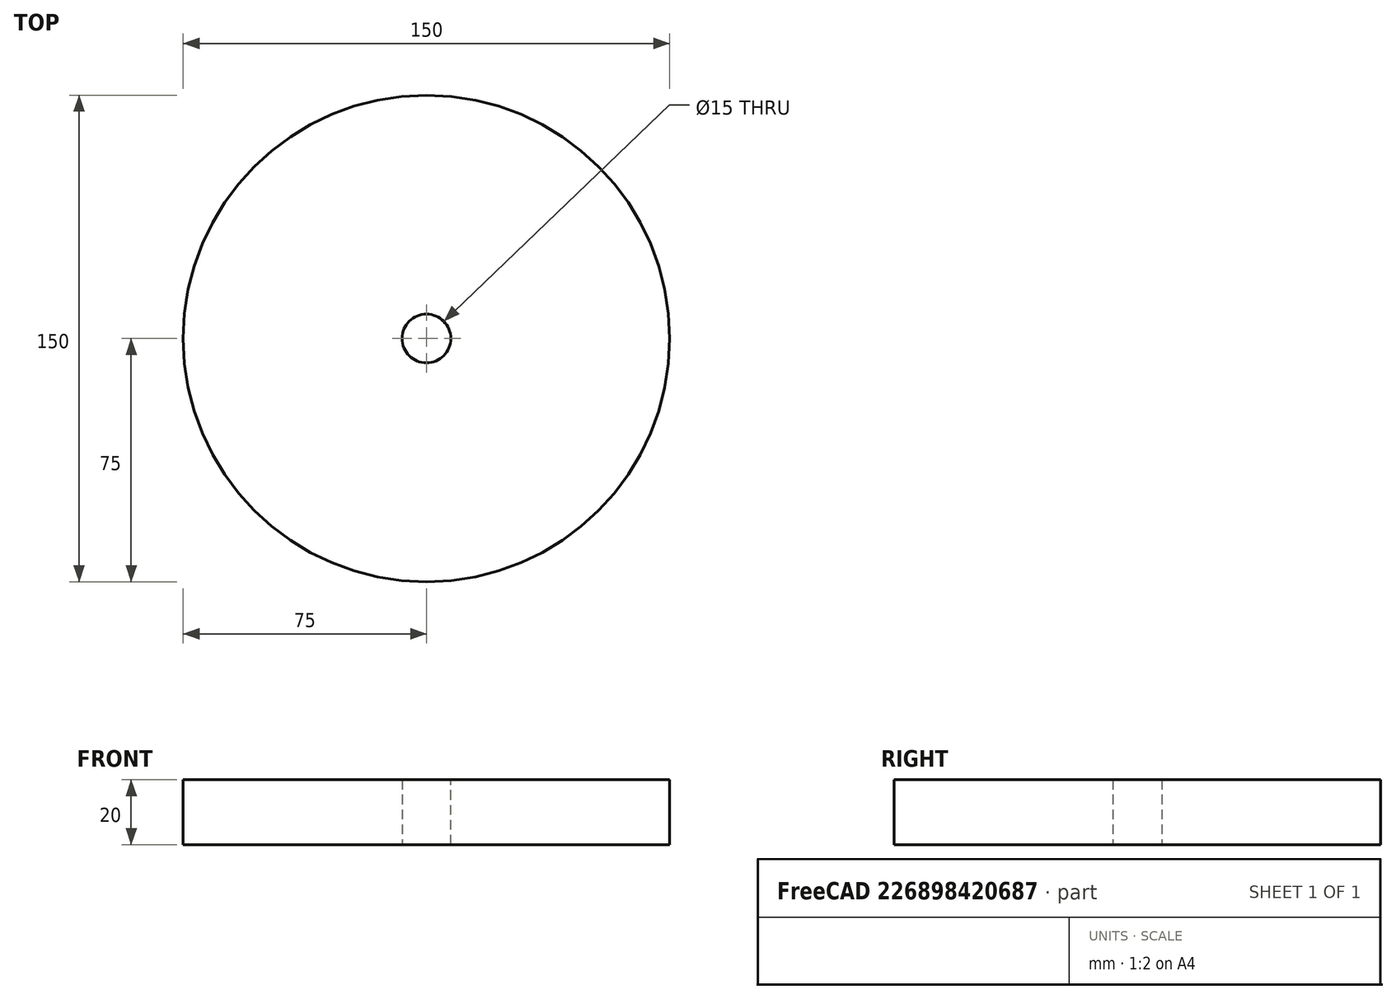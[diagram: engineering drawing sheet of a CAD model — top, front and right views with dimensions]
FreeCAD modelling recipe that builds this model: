
FCSTD DOCUMENT  (FreeCAD 0.18R4 (GitTag))
Label: Base
License: All rights reserved
LicenseURL: http://en.wikipedia.org/wiki/All_rights_reserved
objects: Drawing::FeatureViewPart×3, App::Part×1, Sketcher::SketchObject×1, PartDesign::Pad×1, PartDesign::Body×1, Drawing::FeaturePage×1, Part::Feature×1
note: 5 computed .brp shape members not serialized (recipe doc carries the construction recipe); baked Part::Feature solids carry a one-line shape summary decoded from their .brp

FEATURE [App::Part] Part  label="Base"
  Origin = -> Origin
FEATURE [Sketcher::SketchObject] Sketch
  MapMode = 5
  Support = -> [XY_Plane001]
  sketch-geometry (2):
    g0: Circle CenterX=0 CenterY=0 CenterZ=0 NormalX=0 NormalY=0 NormalZ=1 AngleXU=0 Radius=75
    g1: Circle CenterX=0 CenterY=0 CenterZ=0 NormalX=0 NormalY=0 NormalZ=1 AngleXU=0 Radius=7.5
  constraints (4):
    c: Coincident(g0,g-1)
    c: Coincident(g1,g0)
    c: Diameter(g1) = 15
    c: Diameter(g0) = 150
FEATURE [PartDesign::Pad] Pad
  Length = 20
  Length2 = 100
  Profile = -> Sketch
  Type = 0
FEATURE [PartDesign::Body] Body
  Group = -> [Sketch,Pad]
  Origin = -> Origin001
  Tip = -> Pad
FEATURE [Drawing::FeatureViewPart] Ortho  label="Ortho_0_0"
  Direction = (1,0,0)
  HiddenWidth = 0.15
  LineWidth = 0.35
  Rotation = -90
  ShowHiddenLines = true
  ShowSmoothLines = false
  Source = -> Body
  Tolerance = 0.05
  ViewResult = <blob: 3359 chars omitted>
  Visible = false
  X = 118.36
  Y = 211.298
FEATURE [Drawing::FeatureViewPart] Ortho001  label="Ortho_0_1"
  Direction = (0,0,1)
  HiddenWidth = 0.15
  LineWidth = 0.35
  Rotation = 90
  ShowHiddenLines = true
  ShowSmoothLines = false
  Source = -> Body
  Tolerance = 0.05
  ViewResult = <g id="Ortho_0_1"\n   transform="rotate(90,118.36,100.596) translate(118.36,100.596) scale(1,1)"\n  >\n<g   fill="none"\n   stroke="rgb(0, 0, 0)"\n   stroke-dasharray="0.2,0.1)"\n   stroke-linecap="butt"\n   stroke-linejoin="miter"\n   stroke-width="0.150000"\n   transform="scale(1,-1)"\n  >\n<circle cx ="0" cy ="0" r ="75" /><circle cx ="0" cy ="0" r ="7.5" /></g>\n<g   fill="none"\n   stroke="rgb(0, 0, 0)"\n   stroke-linecap="butt"\n   stroke-linejoin="miter"\n   stroke-width="0.350000"\n   transform="scale(1,-1)"\n  >\n<circle cx ="0" cy ="0" r ="75" /><circle cx ="0" cy ="0" r ="7.5" /></g>\n</g>
  Visible = false
  X = 118.36
  Y = 100.596
FEATURE [Drawing::FeatureViewPart] Ortho002  label="Ortho_1_1"
  Direction = (0.57735,0.57735,0.57735)
  HiddenWidth = 0.15
  LineWidth = 0.35
  Rotation = 120
  ShowHiddenLines = true
  ShowSmoothLines = false
  Source = -> Body
  Tolerance = 0.05
  ViewResult = <g id="Ortho_1_1"\n   transform="rotate(120,301.704,108.792) translate(301.704,108.792) scale(1,1)"\n  >\n<g   fill="none"\n   stroke="rgb(0, 0, 0)"\n   stroke-dasharray="0.2,0.1)"\n   stroke-linecap="butt"\n   stroke-linejoin="miter"\n   stroke-width="0.150000"\n   transform="scale(1,-1)"\n  >\n<path d="M-37.5 64.9519 A75 43.3013 120 0 1 37.5 -64.9519" />\n<path d="M5.3033 -3.06186 A7.5 4.33013 120 0 1 -3.75 6.49519" />\n<path d="M-3.75 6.49519 A7.5 4.33013 120 0 1 3.75 -6.49519" />\n<path d="M3.75 -6.49519 A7.5 4.33013 120 0 1 5.3033 -3.06186" />\n</g>\n<g   fill="none"\n   stroke="rgb(0, 0, 0)"\n   stroke-dasharray="0.02,0.1)"\n   stroke-linecap="butt"\n   stroke-linejoin="miter"\n   stroke-width="0.150000"\n   transform="scale(1,-1)"\n  >\n<path id= "1" d=" M -10.3921 -14.6602 L 3.75 -6.49519 " />\n<path id= "2" d=" M -17.8921 -1.66978 L -3.75 6.49519 " />\n</g>\n<g   fill="none"\n   stroke="rgb(0, 0, 0)"\n   stroke-linecap="butt"\n   stroke-linejoin="miter"\n   stroke-width="0.350000"\n   transform="scale(1,-1)"\n  >\n<path id= "1" d=" M 23.3579 -73.1169 L 37.5 -64.9519 " />\n<path id= "2" d=" M -51.6421 56.7869 L -37.5 64.9519 " />\n</g>\n<g   fill="none"\n   stroke="rgb(0, 0, 0)"\n   stroke-linecap="butt"\n   stroke-linejoin="miter"\n   stroke-width="0.350000"\n   transform="scale(1,-1)"\n  >\n<path d="M53.033 -30.6186 A75 43.3013 120 0 1 -37.5 64.9519" />\n<path d="M37.5 -64.9519 A75 43.3013 120 0 1 53.033 -30.6186" />\n<path d="M38.8909 -38.7836 A75 43.3013 120 0 1 -51.6421 56.7869" />\n<path d="M-51.6421 56.7869 A75 43.3013 120 0 1 23.3579 -73.1169" />\n<path d="M23.3579 -73.1169 A75 43.3013 120 0 1 38.8909 -38.7836" />\n<path d="M-8.83883 -11.2268 A7.5 4.33013 120 0 1 -17.8921 -1.66978" />\n<path d="M-17.8921 -1.66978 A7.5 4.33013 120 0 1 -10.3921 -14.6602" />\n<path d="M-10.3921 -14.6602 A7.5 4.33013 120 0 1 -8.83883 -11.2268" />\n</g>\n</g>
  Visible = false
  X = 301.704
  Y = 108.792
FEATURE [Drawing::FeaturePage] Page
  EditableTexts = L. Cañamar Amaya | March 19, 2021 | A. A. Pech Che | 1:1 | 7 | 1 | Base | base platform
  Group = -> [Ortho,Ortho001,Ortho002]
  Template = D:/Installed Programs/FreeCAD 0.18/data/Mod/Drawing/Templates/A3_Landscape.svg
FEATURE [Part::Feature] Pad001  label="Robot_Base"
  shape: bbox 150 x 150 x 20 mm, 4 faces (baked)
